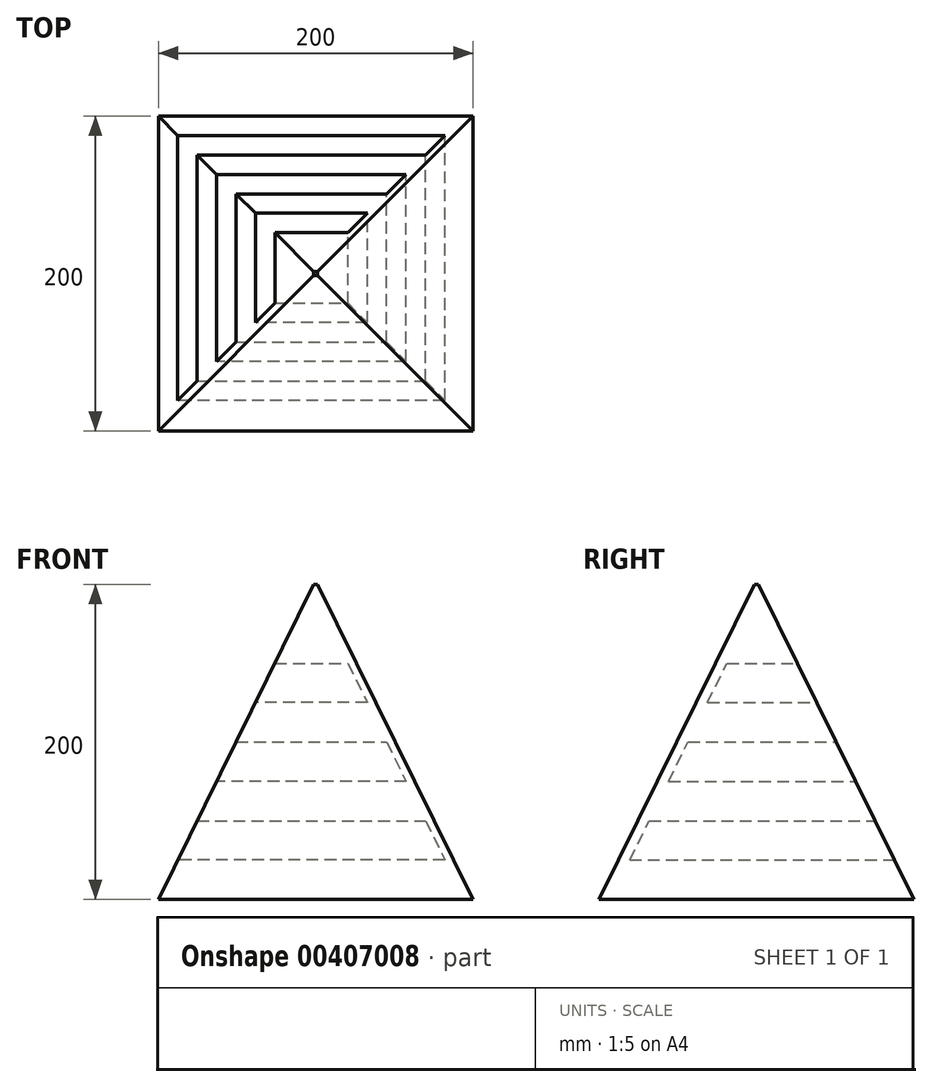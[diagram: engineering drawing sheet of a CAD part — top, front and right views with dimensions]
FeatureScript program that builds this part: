
annotation { "Feature Type Name" : "Feature", "Feature Type Description" : "" }
export const myFeature = defineFeature(function(context is Context, id is Id, definition is map)
    precondition{}
    {
        {
            var Q0;
            Q0=qCreatedBy(makeId("Top.planeOp"),FACE);
            var sketch = newSketch(context, id + "F0", { "sketchPlane" : qUnion([Q0])});
            skLineSegment(sketch, "E0.bottom", {"start": v(100, 100) * mm, "end": v(-100, 100) * mm});
            skLineSegment(sketch, "E0.top", {"start": v(100, -100) * mm, "end": v(-100, -100) * mm});
            skLineSegment(sketch, "E0.left", {"start": v(100, 100) * mm, "end": v(100, -100) * mm});
            skLineSegment(sketch, "E0.right", {"start": v(-100, 100) * mm, "end": v(-100, -100) * mm});
            skPoint(sketch, "E0.middle", {"position": v(0, 0) * mm});
            skSolve(sketch);
        }
        {
            var Q0;
            Q0=qCreatedBy(makeId("Top.planeOp"),FACE);
            cPlane(context, id + "F1", {"entities" : qUnion([Q0]), "cplaneType" : CPlaneType.OFFSET, "offset" : 200 * mm, "width" : 152.4 * mm, "height" : 152.4 * mm});
        }
        {
            var Q0;
            Q0=qCreatedBy(id+"F1.planeOp",FACE);
            var sketch = newSketch(context, id + "F2", { "sketchPlane" : qUnion([Q0])});
            skLineSegment(sketch, "E1.bottom", {"start": v(1.27, 1.27) * mm, "end": v(-1.27, 1.27) * mm});
            skLineSegment(sketch, "E1.top", {"start": v(1.27, -1.27) * mm, "end": v(-1.27, -1.27) * mm});
            skLineSegment(sketch, "E1.left", {"start": v(1.27, 1.27) * mm, "end": v(1.27, -1.27) * mm});
            skLineSegment(sketch, "E1.right", {"start": v(-1.27, 1.27) * mm, "end": v(-1.27, -1.27) * mm});
            skPoint(sketch, "E1.middle", {"position": v(0, 0) * mm});
            skSolve(sketch);
        }
        {
            var Q0;
            Q0=makeQuery(id+"F0.imprint","IMPRINT",FACE,{"disambiguationData":[TD([[makeQuery(id+"F0.imprint","IMPRINT",EDGE,{"derivedFrom":sQuery(id+"F0.wireOp",EDGE,"E0.bottom")}),1.0]])]});
            var Q1;
            Q1=makeQuery(id+"F2.imprint","IMPRINT",FACE,{"disambiguationData":[TD([[makeQuery(id+"F2.imprint","IMPRINT",EDGE,{"derivedFrom":sQuery(id+"F2.wireOp",EDGE,"E1.bottom")}),1.0]])]});
            var Q2;
            Q2=sQuery(id+"F2.wireOp",VERTEX,"E1.left.end");
            var Q3;
            Q3=sQuery(id+"F0.wireOp",VERTEX,"E0.bottom.start");
            loft(context, id + "F3", {"sheetProfilesArray" : [{ "sheetProfileEntities" : qUnion([Q0]) }, { "sheetProfileEntities" : qUnion([Q1]) }], "connections" : [{ "connectionEntities" : qUnion([Q2, Q3]), "connectionEdgeQueries" : qUnion([]), "connectionEdgeParameters" : [] }]});
        }
        {
            var Q0;
            Q0=qCreatedBy(makeId("Front.planeOp"),FACE);
            var Q1;
            Q1=makeQuery(id+"F3.opLoft","MID_CAP_VERTEX",VERTEX,{"disambiguationData":[OSD([sQuery(id+"F0.wireOp",EDGE,"E0.bottom"),sQuery(id+"F0.wireOp",EDGE,"E0.left")])],"capPos":0.0});
            cPlane(context, id + "F4", {"entities" : qUnion([Q0, Q1]), "cplaneType" : CPlaneType.PLANE_POINT, "offset" : 25.4 * mm, "width" : 152.4 * mm, "height" : 152.4 * mm});
        }
        {
            var Q0;
            Q0=qCreatedBy(id+"F4.planeOp",FACE);
            var sketch = newSketch(context, id + "F5", { "sketchPlane" : qUnion([Q0])});
            skLineSegment(sketch, "E2", {"start": v(-87.66, 25) * mm, "end": v(-87.66, 50) * mm});
            skLineSegment(sketch, "E3", {"start": v(-87.66, 50) * mm, "end": v(69.74, 50) * mm});
            skLineSegment(sketch, "E4", {"start": v(69.74, 50) * mm, "end": v(82.08, 25) * mm});
            skLineSegment(sketch, "E5", {"start": v(82.08, 25) * mm, "end": v(-87.66, 25) * mm});
            skLineSegment(sketch, "E6", {"start": v(-62.98, 75) * mm, "end": v(-62.98, 100) * mm});
            skLineSegment(sketch, "E7", {"start": v(-62.98, 100) * mm, "end": v(45.06, 100) * mm});
            skLineSegment(sketch, "E8", {"start": v(45.06, 100) * mm, "end": v(57.4, 75) * mm});
            skLineSegment(sketch, "E9", {"start": v(57.4, 75) * mm, "end": v(-62.98, 75) * mm});
            skLineSegment(sketch, "E10", {"start": v(-38.3, 125) * mm, "end": v(-38.3, 150) * mm});
            skLineSegment(sketch, "E11", {"start": v(-38.3, 150) * mm, "end": v(20.38, 150) * mm});
            skLineSegment(sketch, "E12", {"start": v(20.38, 150) * mm, "end": v(32.72, 125) * mm});
            skLineSegment(sketch, "E13", {"start": v(32.72, 125) * mm, "end": v(-38.3, 125) * mm});
            skSolve(sketch);
        }
        {
            var Q0;
            {var subQ0=sQuery(id+"F2.wireOp",EDGE,"E1.left");var subQ1=sQuery(id+"F2.wireOp",EDGE,"E1.top");var subQ3=sQuery(id+"F0.wireOp",EDGE,"E0.left");var subQ4=sQuery(id+"F0.wireOp",EDGE,"E0.top");var subQ6=sQuery(id+"F2.wireOp",EDGE,"E1.right");var subQ7=sQuery(id+"F0.wireOp",EDGE,"E0.right");Q0=makeQuery(id+"F7.boolean.opBoolean","SPLIT",FACE,{"disambiguationData":[TD([makeQuery(id+"F7.opExtrude","SWEPT_FACE",FACE,{"disambiguationData":[OSD([sQuery(id+"F5.wireOp",EDGE,"E7")])]})])],"derivedFrom":makeQuery(id+"F3.opLoft","SWEPT_FACE",FACE,{"disambiguationData":[OSD([subQ4,subQ3,subQ7,subQ1,subQ0,subQ6])]})});}
            cPlane(context, id + "F6", {"entities" : qUnion([Q0]), "cplaneType" : CPlaneType.OFFSET, "offset" : 6.35 * mm, "oppositeDirection" : true, "width" : 152.4 * mm, "height" : 152.4 * mm});
        }
        {
            var Q0;
            Q0=makeQuery(id+"F5.imprint","IMPRINT",FACE,{"disambiguationData":[TD([[makeQuery(id+"F5.imprint","IMPRINT",EDGE,{"derivedFrom":sQuery(id+"F5.wireOp",EDGE,"E10")}),-1.0]])]});
            var Q1;
            Q1=makeQuery(id+"F5.imprint","IMPRINT",FACE,{"disambiguationData":[TD([[makeQuery(id+"F5.imprint","IMPRINT",EDGE,{"derivedFrom":sQuery(id+"F5.wireOp",EDGE,"E6")}),-1.0]])]});
            var Q2;
            Q2=makeQuery(id+"F5.imprint","IMPRINT",FACE,{"disambiguationData":[TD([[makeQuery(id+"F5.imprint","IMPRINT",EDGE,{"derivedFrom":sQuery(id+"F5.wireOp",EDGE,"E2")}),-1.0]])]});
            var Q3;
            Q3=qCreatedBy(id+"F6.planeOp",FACE);
            extrude(context, id + "F7", {"entities" : qUnion([Q0, Q1, Q2]), "operationType" : NewBodyOperationType.REMOVE, "endBound" : BoundingType.UP_TO_SURFACE, "endBoundEntityFace" : qUnion([Q3]), "offsetDistance" : 25 * mm, "depth" : 38.1 * mm});
        }
    });
